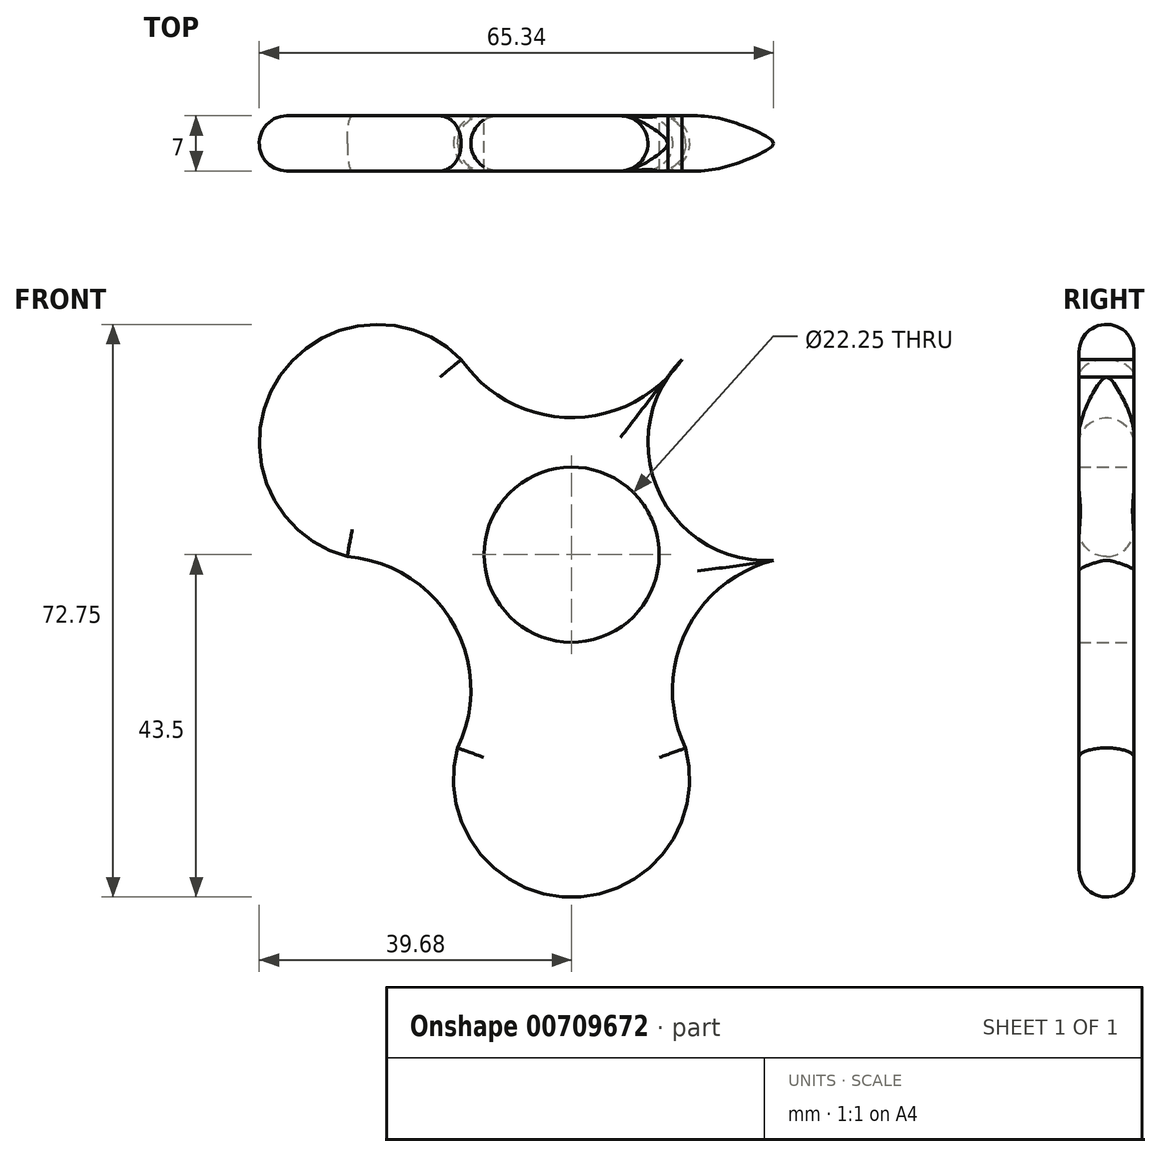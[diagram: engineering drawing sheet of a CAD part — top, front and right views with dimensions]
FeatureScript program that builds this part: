
annotation { "Feature Type Name" : "Feature", "Feature Type Description" : "" }
export const myFeature = defineFeature(function(context is Context, id is Id, definition is map)
    precondition{}
    {
        {
            var Q0;
            Q0=qCreatedBy(makeId("Front.planeOp"),FACE);
            var sketch = newSketch(context, id + "F0", { "sketchPlane" : qUnion([Q0])});
            skCircle(sketch, "E0", {"center": v(0, 0) * mm, "radius": 11.12 * mm});
            skCircle(sketch, "E1", {"center": v(0, -28.5) * mm, "radius": 15 * mm});
            skCircle(sketch, "E2.1.1", {"center": v(24.68, 14.25) * mm, "radius": 15 * mm});
            skCircle(sketch, "E2.2.1", {"center": v(-24.68, 14.25) * mm, "radius": 15 * mm});
            skArc(sketch, "E3", {"start": v(-14.47, -24.55) * mm, "mid": v(-15.08, -8.7) * mm, "end": v(-28.5, -0.26) * mm});
            skArc(sketch, "E4", {"start": v(28.5, -0.26) * mm, "mid": v(15.08, -8.7) * mm, "end": v(14.47, -24.55) * mm});
            skArc(sketch, "E5", {"start": v(-14.03, 24.8) * mm, "mid": v(0, 17.41) * mm, "end": v(14.03, 24.8) * mm});
            skSolve(sketch);
        }
        {
            var Q0;
            {var subQ0=sQuery(id+"F0.wireOp",EDGE,"E3");var subQ1=sQuery(id+"F0.wireOp",EDGE,"E2.2.1");var subQ2=makeQuery(id+"F0.imprint","INTERSECT",VERTEX,{"disambiguationData":[OD(1.0)],"derivedFrom":[subQ1,subQ0]});Q0=makeQuery(id+"F0.imprint","IMPRINT",FACE,{"disambiguationData":[TD([[makeQuery(id+"F0.imprint","IMPRINT",EDGE,{"disambiguationData":[TD([[subQ2,-1.0]])],"derivedFrom":subQ1}),1.0]])]});}
            var Q1;
            Q1=makeQuery(id+"F0.imprint","IMPRINT",FACE,{"disambiguationData":[TD([[makeQuery(id+"F0.imprint","IMPRINT",EDGE,{"derivedFrom":sQuery(id+"F0.wireOp",EDGE,"E0")}),-1.0]])]});
            var Q2;
            {var subQ0=sQuery(id+"F0.wireOp",EDGE,"E5");var subQ1=sQuery(id+"F0.wireOp",EDGE,"E2.1.1");var subQ2=makeQuery(id+"F0.imprint","INTERSECT",VERTEX,{"disambiguationData":[OD(1.0)],"derivedFrom":[subQ1,subQ0]});Q2=makeQuery(id+"F0.imprint","IMPRINT",FACE,{"disambiguationData":[TD([[makeQuery(id+"F0.imprint","IMPRINT",EDGE,{"disambiguationData":[TD([[subQ2,-1.0]])],"derivedFrom":subQ1}),1.0]])]});}
            var Q3;
            {var subQ0=sQuery(id+"F0.wireOp",EDGE,"E4");var subQ1=sQuery(id+"F0.wireOp",EDGE,"E1");var subQ2=makeQuery(id+"F0.imprint","INTERSECT",VERTEX,{"disambiguationData":[OD(1.0)],"derivedFrom":[subQ1,subQ0]});Q3=makeQuery(id+"F0.imprint","IMPRINT",FACE,{"disambiguationData":[TD([[makeQuery(id+"F0.imprint","IMPRINT",EDGE,{"disambiguationData":[TD([[subQ2,-1.0]])],"derivedFrom":subQ1}),1.0]])]});}
            extrude(context, id + "F1", {"entities" : qUnion([Q0, Q1, Q2, Q3]), "depth" : 7 * mm, "offsetDistance" : 25 * mm});
        }
        {
            var Q0;
            Q0=makeQuery(id+"F1.opExtrude","CAP_EDGE",EDGE,{"disambiguationData":[OSD([sQuery(id+"F0.wireOp",EDGE,"E3")])],"isStart":true});
            var Q1;
            Q1=makeQuery(id+"F1.opExtrude","CAP_EDGE",EDGE,{"disambiguationData":[OSD([sQuery(id+"F0.wireOp",EDGE,"E1")])],"isStart":true});
            var Q2;
            Q2=makeQuery(id+"F1.opExtrude","CAP_EDGE",EDGE,{"disambiguationData":[OSD([sQuery(id+"F0.wireOp",EDGE,"E4")])],"isStart":true});
            var Q3;
            Q3=makeQuery(id+"F1.opExtrude","CAP_EDGE",EDGE,{"disambiguationData":[OSD([sQuery(id+"F0.wireOp",EDGE,"E2.1.1")])],"isStart":true});
            var Q4;
            Q4=makeQuery(id+"F1.opExtrude","CAP_EDGE",EDGE,{"disambiguationData":[OSD([sQuery(id+"F0.wireOp",EDGE,"E5")])],"isStart":true});
            var Q5;
            Q5=makeQuery(id+"F1.opExtrude","CAP_EDGE",EDGE,{"disambiguationData":[OSD([sQuery(id+"F0.wireOp",EDGE,"E2.2.1")])],"isStart":true});
            var Q6;
            Q6=makeQuery(id+"F1.opExtrude","CAP_EDGE",EDGE,{"disambiguationData":[OSD([sQuery(id+"F0.wireOp",EDGE,"E5")])],"isStart":false});
            var Q7;
            Q7=makeQuery(id+"F1.opExtrude","CAP_EDGE",EDGE,{"disambiguationData":[OSD([sQuery(id+"F0.wireOp",EDGE,"E2.2.1")])],"isStart":false});
            var Q8;
            Q8=makeQuery(id+"F1.opExtrude","CAP_EDGE",EDGE,{"disambiguationData":[OSD([sQuery(id+"F0.wireOp",EDGE,"E3")])],"isStart":false});
            var Q9;
            Q9=makeQuery(id+"F1.opExtrude","CAP_EDGE",EDGE,{"disambiguationData":[OSD([sQuery(id+"F0.wireOp",EDGE,"E1")])],"isStart":false});
            var Q10;
            Q10=makeQuery(id+"F1.opExtrude","CAP_EDGE",EDGE,{"disambiguationData":[OSD([sQuery(id+"F0.wireOp",EDGE,"E4")])],"isStart":false});
            var Q11;
            Q11=makeQuery(id+"F1.opExtrude","CAP_EDGE",EDGE,{"disambiguationData":[OSD([sQuery(id+"F0.wireOp",EDGE,"E2.1.1")])],"isStart":false});
            fillet(context, id + "F2", {"entities" : qUnion([Q0, Q1, Q2, Q3, Q4, Q5, Q6, Q7, Q8, Q9, Q10, Q11]), "radius" : 3.5 * mm, "tangentPropagation" : true, "allowEdgeOverflow" : false});
        }
    });
